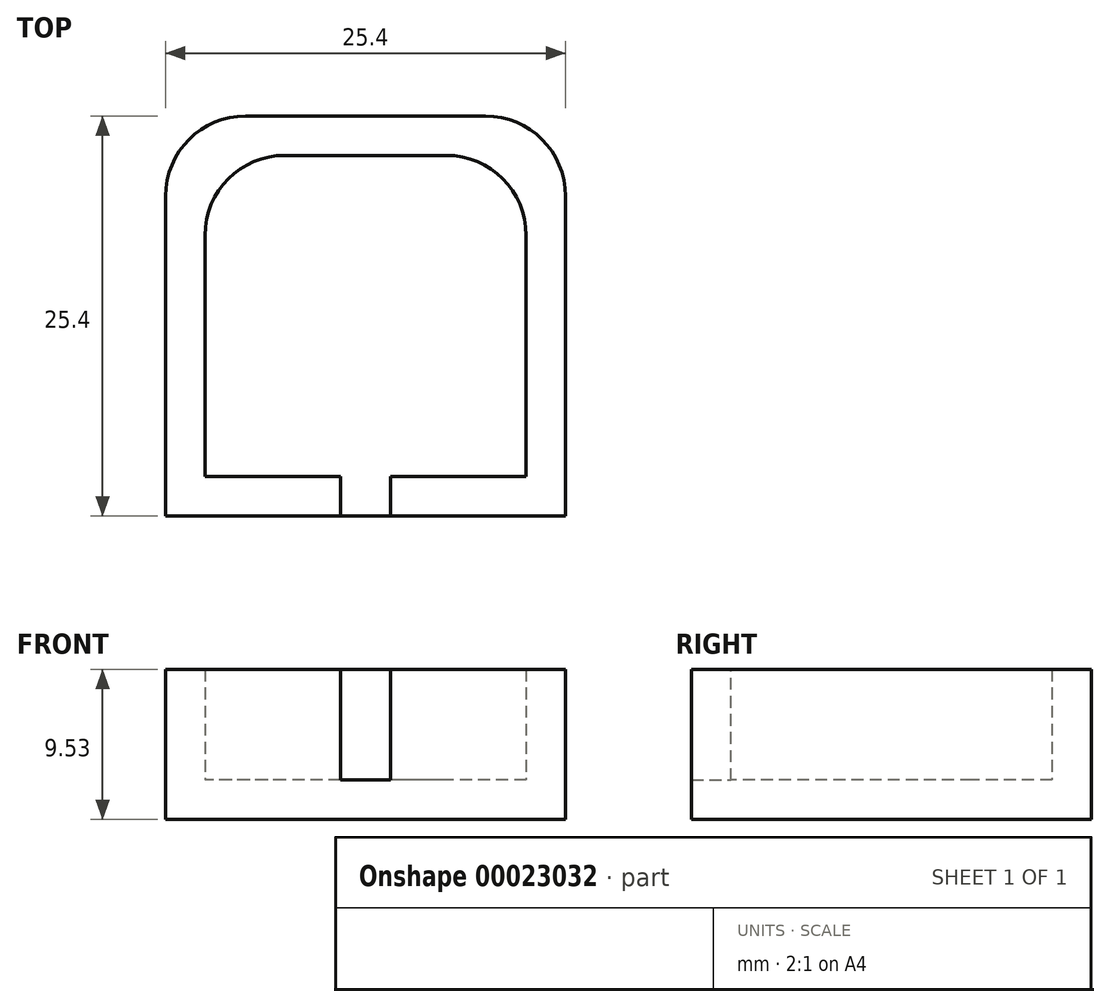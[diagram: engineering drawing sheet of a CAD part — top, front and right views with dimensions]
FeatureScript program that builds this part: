
annotation { "Feature Type Name" : "Feature", "Feature Type Description" : "" }
export const myFeature = defineFeature(function(context is Context, id is Id, definition is map)
    precondition{}
    {
        {
            var Q0;
            Q0=qCreatedBy(makeId("Top.planeOp"),FACE);
            var sketch = newSketch(context, id + "F0", { "sketchPlane" : qUnion([Q0])});
            skLineSegment(sketch, "E0.rect.bottom", {"start": v(12.7, 12.7) * mm, "end": v(-12.7, 12.7) * mm});
            skLineSegment(sketch, "E0.rect.top", {"start": v(12.7, -12.7) * mm, "end": v(-12.7, -12.7) * mm});
            skLineSegment(sketch, "E0.rect.left", {"start": v(12.7, 12.7) * mm, "end": v(12.7, -12.7) * mm});
            skLineSegment(sketch, "E0.rect.right", {"start": v(-12.7, 12.7) * mm, "end": v(-12.7, -12.7) * mm});
            skPoint(sketch, "E0.rect.middle", {"position": v(0, 0) * mm});
            skSolve(sketch);
        }
        {
            var Q0;
            Q0 = qSketchRegion(id + "F0", true);
            extrude(context, id + "F1", {"entities" : qUnion([Q0]), "depth" : 9.52 * mm});
        }
        {
            var Q0;
            Q0=makeQuery(id+"F1.opExtrude","CAP_FACE",FACE,{"disambiguationData":[OSD([sQuery(id+"F0.wireOp",EDGE,"E0.rect.bottom"),sQuery(id+"F0.wireOp",EDGE,"E0.rect.top"),sQuery(id+"F0.wireOp",EDGE,"E0.rect.left"),sQuery(id+"F0.wireOp",EDGE,"E0.rect.right")])],"isStart":false});
            shell(context, id + "F2", {"entities" : qUnion([Q0]), "thickness" : 2.5 * mm});
        }
        {
            var Q0;
            Q0=makeQuery(id+"F1.opExtrude","SWEPT_EDGE",EDGE,{"disambiguationData":[OSD([sQuery(id+"F0.wireOp",EDGE,"E0.rect.bottom"),sQuery(id+"F0.wireOp",EDGE,"E0.rect.left")])]});
            var Q1;
            Q1=makeQuery(id+"F1.opExtrude","SWEPT_EDGE",EDGE,{"disambiguationData":[OSD([sQuery(id+"F0.wireOp",EDGE,"E0.rect.bottom"),sQuery(id+"F0.wireOp",EDGE,"E0.rect.right")])]});
            var Q2;
            Q2=makeQuery(id+"F2.opShell","OFFSET_EDGE",EDGE,{"disambiguationData":[OSD([sQuery(id+"F0.wireOp",EDGE,"E0.rect.bottom"),sQuery(id+"F0.wireOp",EDGE,"E0.rect.left")])]});
            var Q3;
            Q3=makeQuery(id+"F2.opShell","OFFSET_EDGE",EDGE,{"disambiguationData":[OSD([sQuery(id+"F0.wireOp",EDGE,"E0.rect.bottom"),sQuery(id+"F0.wireOp",EDGE,"E0.rect.right")])]});
            fillet(context, id + "F3", {"entities" : qUnion([Q0, Q1, Q2, Q3]), "radius" : 5.08 * mm, "tangentPropagation" : true, "allowEdgeOverflow" : false});
        }
        {
            var Q0;
            Q0=makeQuery(id+"F1.opExtrude","CAP_FACE",FACE,{"disambiguationData":[OSD([sQuery(id+"F0.wireOp",EDGE,"E0.rect.bottom"),sQuery(id+"F0.wireOp",EDGE,"E0.rect.top"),sQuery(id+"F0.wireOp",EDGE,"E0.rect.left"),sQuery(id+"F0.wireOp",EDGE,"E0.rect.right")])],"isStart":false});
            var sketch = newSketch(context, id + "F4", { "sketchPlane" : qUnion([Q0])});
            skLineSegment(sketch, "E1.rect.bottom", {"start": v(1.59, -10.2) * mm, "end": v(-1.59, -10.2) * mm});
            skLineSegment(sketch, "E1.rect.top", {"start": v(1.59, -12.7) * mm, "end": v(-1.59, -12.7) * mm});
            skLineSegment(sketch, "E1.rect.left", {"start": v(1.59, -10.2) * mm, "end": v(1.59, -12.7) * mm});
            skLineSegment(sketch, "E1.rect.right", {"start": v(-1.59, -10.2) * mm, "end": v(-1.59, -12.7) * mm});
            skPoint(sketch, "E1.rect.middle", {"position": v(0, -11.45) * mm});
            skSolve(sketch);
        }
        {
            var Q0;
            Q0 = qSketchRegion(id + "F4", true);
            var Q1;
            Q1=makeQuery(id+"F2.opShell","OFFSET_FACE",FACE,{"disambiguationData":[OSD([sQuery(id+"F0.wireOp",EDGE,"E0.rect.bottom"),sQuery(id+"F0.wireOp",EDGE,"E0.rect.top"),sQuery(id+"F0.wireOp",EDGE,"E0.rect.left"),sQuery(id+"F0.wireOp",EDGE,"E0.rect.right")])]});
            extrude(context, id + "F5", {"entities" : qUnion([Q0]), "operationType" : NewBodyOperationType.REMOVE, "endBound" : BoundingType.UP_TO_SURFACE, "oppositeDirection" : true, "endBoundEntityFace" : qUnion([Q1]), "depth" : 25.4 * mm});
        }
    });
